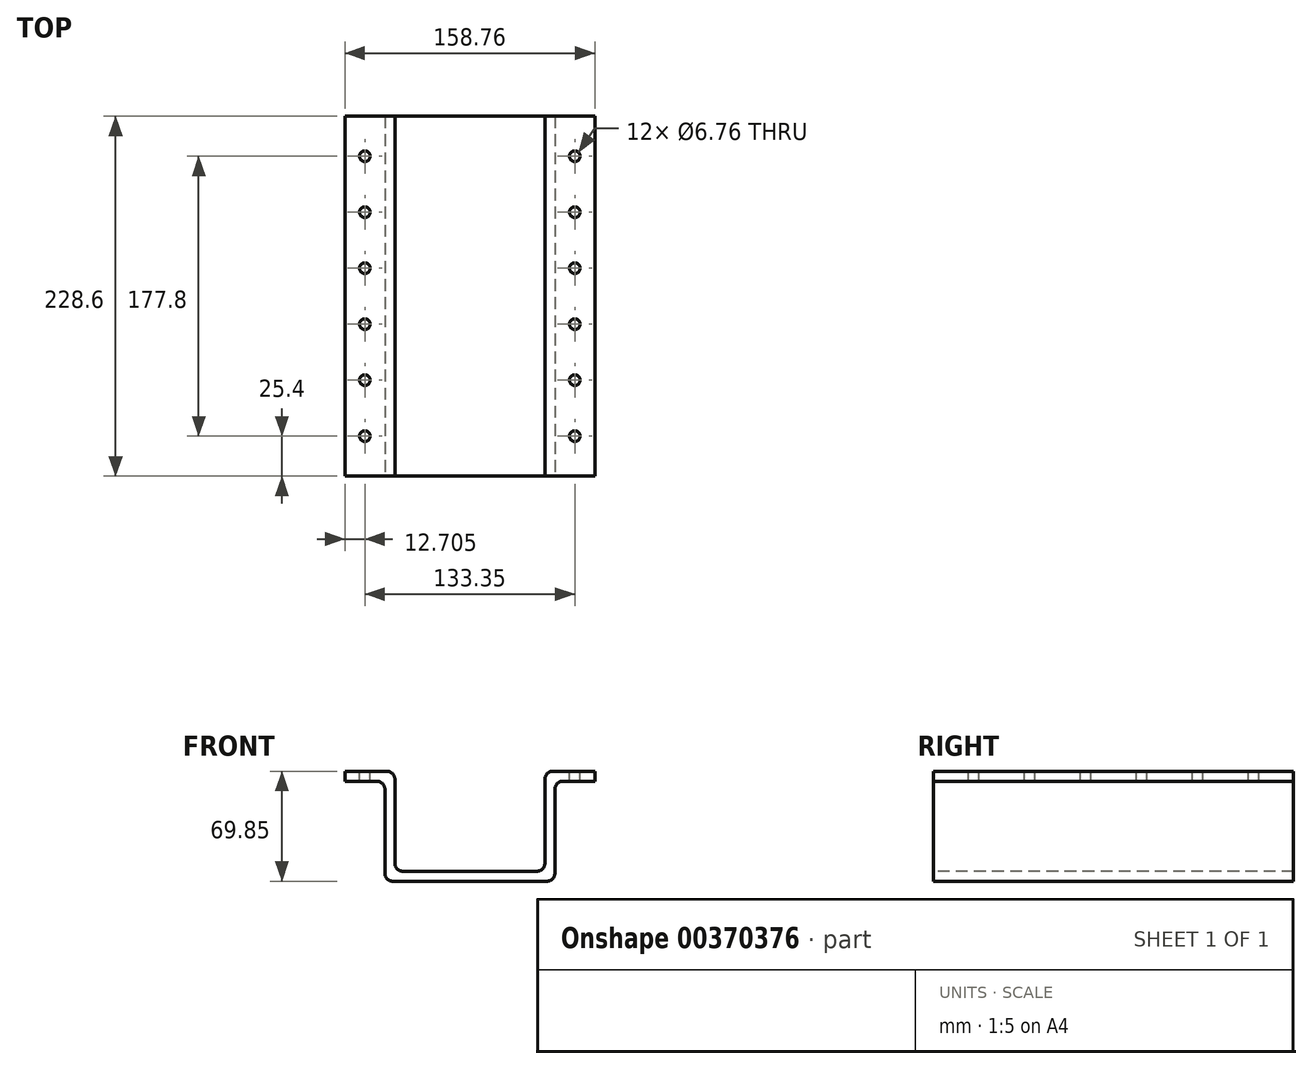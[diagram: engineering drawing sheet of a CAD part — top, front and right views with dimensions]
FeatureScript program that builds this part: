
annotation { "Feature Type Name" : "Feature", "Feature Type Description" : "" }
export const myFeature = defineFeature(function(context is Context, id is Id, definition is map)
    precondition{}
    {
        {
            var Q0;
            Q0=qCreatedBy(makeId("Front.planeOp"),FACE);
            var sketch = newSketch(context, id + "F0", { "sketchPlane" : qUnion([Q0])});
            skLineSegment(sketch, "E0", {"start": v(-53.98, 0) * mm, "end": v(53.98, 0) * mm});
            skLineSegment(sketch, "E1", {"start": v(-53.98, 0) * mm, "end": v(-53.97, 63.5) * mm});
            skLineSegment(sketch, "E2", {"start": v(-53.98, 63.5) * mm, "end": v(-79.38, 63.5) * mm});
            skLineSegment(sketch, "E3", {"start": v(-79.38, 63.5) * mm, "end": v(-79.38, 69.85) * mm});
            skLineSegment(sketch, "E4", {"start": v(-79.38, 69.85) * mm, "end": v(-47.63, 69.85) * mm});
            skLineSegment(sketch, "E5", {"start": v(-47.62, 69.85) * mm, "end": v(-47.62, 6.35) * mm});
            skLineSegment(sketch, "E6.MirrorCS", {"start": v(79.38, 63.5) * mm, "end": v(79.38, 69.85) * mm});
            skLineSegment(sketch, "E7.MirrorCS", {"start": v(53.98, 63.5) * mm, "end": v(79.38, 63.5) * mm});
            skLineSegment(sketch, "E8.MirrorCS", {"start": v(53.97, 0) * mm, "end": v(53.97, 63.5) * mm});
            skLineSegment(sketch, "E9.MirrorCS", {"start": v(47.62, 69.85) * mm, "end": v(47.62, 6.35) * mm});
            skLineSegment(sketch, "E10.MirrorCS", {"start": v(79.38, 69.85) * mm, "end": v(47.63, 69.85) * mm});
            skLineSegment(sketch, "E11", {"start": v(-47.62, 6.35) * mm, "end": v(47.62, 6.35) * mm});
            skSolve(sketch);
        }
        {
            var Q0;
            Q0=makeQuery(id+"F0.imprint","IMPRINT",FACE,{"disambiguationData":[TD([[makeQuery(id+"F0.imprint","IMPRINT",EDGE,{"derivedFrom":sQuery(id+"F0.wireOp",EDGE,"E0")}),1.0]])]});
            extrude(context, id + "F1", {"entities" : qUnion([Q0]), "oppositeDirection" : true, "depth" : 228.6 * mm});
        }
        {
            var Q0;
            Q0=qCreatedBy(makeId("Front.planeOp"),FACE);
            var sketch = newSketch(context, id + "F2", { "sketchPlane" : qUnion([Q0])});
            skLineSegment(sketch, "E12.0.0", {"start": v(53.97, 63.5) * mm, "end": v(79.38, 63.5) * mm, "construction": true});
            skLineSegment(sketch, "E12.0.1", {"start": v(79.38, 63.5) * mm, "end": v(79.38, 69.85) * mm, "construction": true});
            skLineSegment(sketch, "E12.0.2", {"start": v(79.38, 69.85) * mm, "end": v(47.62, 69.85) * mm, "construction": true});
            skLineSegment(sketch, "E12.0.3", {"start": v(47.62, 69.85) * mm, "end": v(47.62, 6.35) * mm, "construction": true});
            skLineSegment(sketch, "E12.0.4", {"start": v(47.62, 6.35) * mm, "end": v(-47.62, 6.35) * mm, "construction": true});
            skLineSegment(sketch, "E12.0.5", {"start": v(-47.62, 6.35) * mm, "end": v(-47.62, 69.85) * mm, "construction": true});
            skLineSegment(sketch, "E12.0.6", {"start": v(-47.63, 69.85) * mm, "end": v(-79.38, 69.85) * mm, "construction": true});
            skLineSegment(sketch, "E12.0.7", {"start": v(-79.38, 69.85) * mm, "end": v(-79.38, 63.5) * mm, "construction": true});
            skLineSegment(sketch, "E12.0.8", {"start": v(-79.38, 63.5) * mm, "end": v(-53.97, 63.5) * mm, "construction": true});
            skLineSegment(sketch, "E12.0.9", {"start": v(-53.97, 63.5) * mm, "end": v(-53.98, 0) * mm, "construction": true});
            skLineSegment(sketch, "E12.0.10", {"start": v(-53.98, 0) * mm, "end": v(53.98, 0) * mm, "construction": true});
            skLineSegment(sketch, "E12.0.11", {"start": v(53.97, 0) * mm, "end": v(53.97, 63.5) * mm, "construction": true});
            skLineSegment(sketch, "E13", {"start": v(-47.63, 57.15) * mm, "end": v(-18.3, 6.35) * mm});
            skLineSegment(sketch, "E14", {"start": v(-18.3, 6.35) * mm, "end": v(-47.62, 6.35) * mm});
            skLineSegment(sketch, "E15", {"start": v(-47.62, 57.15) * mm, "end": v(-47.62, 6.35) * mm});
            skSolve(sketch);
        }
        {
            var Q0;
            Q0=makeQuery(id+"F1.opExtrude","SWEPT_EDGE",EDGE,{"disambiguationData":[OSD([sQuery(id+"F0.wireOp",EDGE,"E4"),sQuery(id+"F0.wireOp",EDGE,"E5")])]});
            var Q1;
            Q1=makeQuery(id+"F1.opExtrude","SWEPT_EDGE",EDGE,{"disambiguationData":[OSD([sQuery(id+"F0.wireOp",EDGE,"E5"),sQuery(id+"F0.wireOp",EDGE,"E11")])]});
            var Q2;
            Q2=makeQuery(id+"F1.opExtrude","SWEPT_EDGE",EDGE,{"disambiguationData":[OSD([sQuery(id+"F0.wireOp",EDGE,"E0"),sQuery(id+"F0.wireOp",EDGE,"E8.MirrorCS")])]});
            var Q3;
            Q3=makeQuery(id+"F1.opExtrude","SWEPT_EDGE",EDGE,{"disambiguationData":[OSD([sQuery(id+"F0.wireOp",EDGE,"E9.MirrorCS"),sQuery(id+"F0.wireOp",EDGE,"E11")])]});
            var Q4;
            Q4=makeQuery(id+"F1.opExtrude","SWEPT_EDGE",EDGE,{"disambiguationData":[OSD([sQuery(id+"F0.wireOp",EDGE,"E0"),sQuery(id+"F0.wireOp",EDGE,"E1")])]});
            var Q5;
            Q5=makeQuery(id+"F1.opExtrude","SWEPT_EDGE",EDGE,{"disambiguationData":[OSD([sQuery(id+"F0.wireOp",EDGE,"E1"),sQuery(id+"F0.wireOp",EDGE,"E2")])]});
            var Q6;
            Q6=makeQuery(id+"F1.opExtrude","SWEPT_EDGE",EDGE,{"disambiguationData":[OSD([sQuery(id+"F0.wireOp",EDGE,"E7.MirrorCS"),sQuery(id+"F0.wireOp",EDGE,"E8.MirrorCS")])]});
            var Q7;
            Q7=makeQuery(id+"F1.opExtrude","SWEPT_EDGE",EDGE,{"disambiguationData":[OSD([sQuery(id+"F0.wireOp",EDGE,"E9.MirrorCS"),sQuery(id+"F0.wireOp",EDGE,"E10.MirrorCS")])]});
            fillet(context, id + "F3", {"entities" : qUnion([Q0, Q1, Q2, Q3, Q4, Q5, Q6, Q7]), "radius" : 5.08 * mm, "tangentPropagation" : true, "allowEdgeOverflow" : false});
        }
        {
            var Q0;
            Q0=makeQuery(id+"FtHRsgMsJNszQTX_1.boolean.opBoolean","MERGE",FACE,{"derivedFrom":[makeQuery(id+"F1.opExtrude","CAP_FACE",FACE,{"disambiguationData":[OSD([sQuery(id+"F0.wireOp",EDGE,"E0"),sQuery(id+"F0.wireOp",EDGE,"E1"),sQuery(id+"F0.wireOp",EDGE,"E2"),sQuery(id+"F0.wireOp",EDGE,"E3"),sQuery(id+"F0.wireOp",EDGE,"E4"),sQuery(id+"F0.wireOp",EDGE,"E5"),sQuery(id+"F0.wireOp",EDGE,"E6.MirrorCS"),sQuery(id+"F0.wireOp",EDGE,"E7.MirrorCS"),sQuery(id+"F0.wireOp",EDGE,"E8.MirrorCS"),sQuery(id+"F0.wireOp",EDGE,"E9.MirrorCS"),sQuery(id+"F0.wireOp",EDGE,"E10.MirrorCS"),sQuery(id+"F0.wireOp",EDGE,"E11")])],"isStart":true}),makeQuery(id+"FtHRsgMsJNszQTX_1.opExtrude","CAP_FACE",FACE,{"disambiguationData":[OSD([sQuery(id+"F2.wireOp",EDGE,"E13"),sQuery(id+"F2.wireOp",EDGE,"E14"),sQuery(id+"F2.wireOp",EDGE,"E15")])],"isStart":true})]});
            var sketch = newSketch(context, id + "F4", { "sketchPlane" : qUnion([Q0])});
            skLineSegment(sketch, "E16.0.0", {"start": v(-18.3, 6.35) * mm, "end": v(-47.63, 57.15) * mm, "construction": true});
            skLineSegment(sketch, "E16.0.1", {"start": v(-47.62, 57.15) * mm, "end": v(-47.62, 64.77) * mm, "construction": true});
            skArc(sketch, "E16.0.2", {"start": v(-47.62, 64.77) * mm, "mid": v(-49.11, 68.36) * mm, "end": v(-52.7, 69.85) * mm, "construction": true});
            skLineSegment(sketch, "E16.0.3", {"start": v(-52.7, 69.85) * mm, "end": v(-79.38, 69.85) * mm, "construction": true});
            skLineSegment(sketch, "E16.0.4", {"start": v(-79.38, 69.85) * mm, "end": v(-79.38, 63.5) * mm, "construction": true});
            skLineSegment(sketch, "E16.0.5", {"start": v(-79.38, 63.5) * mm, "end": v(-59.05, 63.5) * mm, "construction": true});
            skArc(sketch, "E16.0.6", {"start": v(-59.05, 63.5) * mm, "mid": v(-55.46, 62.01) * mm, "end": v(-53.97, 58.42) * mm, "construction": true});
            skLineSegment(sketch, "E16.0.7", {"start": v(-53.97, 58.42) * mm, "end": v(-53.98, 5.08) * mm, "construction": true});
            skArc(sketch, "E16.0.8", {"start": v(-53.98, 5.08) * mm, "mid": v(-52.49, 1.49) * mm, "end": v(-48.9, 0) * mm, "construction": true});
            skLineSegment(sketch, "E16.0.9", {"start": v(-48.9, 0) * mm, "end": v(48.9, 0) * mm, "construction": true});
            skArc(sketch, "E16.0.10", {"start": v(48.9, 0) * mm, "mid": v(52.49, 1.49) * mm, "end": v(53.97, 5.08) * mm, "construction": true});
            skLineSegment(sketch, "E16.0.11", {"start": v(53.97, 5.08) * mm, "end": v(53.97, 58.42) * mm, "construction": true});
            skArc(sketch, "E16.0.12", {"start": v(53.97, 58.42) * mm, "mid": v(55.46, 62.01) * mm, "end": v(59.05, 63.5) * mm, "construction": true});
            skLineSegment(sketch, "E16.0.13", {"start": v(59.05, 63.5) * mm, "end": v(79.38, 63.5) * mm, "construction": true});
            skLineSegment(sketch, "E16.0.14", {"start": v(79.38, 63.5) * mm, "end": v(79.38, 69.85) * mm, "construction": true});
            skLineSegment(sketch, "E16.0.15", {"start": v(79.38, 69.85) * mm, "end": v(52.7, 69.85) * mm, "construction": true});
            skArc(sketch, "E16.0.16", {"start": v(52.7, 69.85) * mm, "mid": v(49.11, 68.36) * mm, "end": v(47.62, 64.77) * mm, "construction": true});
            skLineSegment(sketch, "E16.0.17", {"start": v(47.62, 64.77) * mm, "end": v(47.62, 11.43) * mm, "construction": true});
            skArc(sketch, "E16.0.18", {"start": v(47.62, 11.43) * mm, "mid": v(46.14, 7.84) * mm, "end": v(42.55, 6.35) * mm, "construction": true});
            skLineSegment(sketch, "E16.0.19", {"start": v(42.55, 6.35) * mm, "end": v(-18.3, 6.35) * mm, "construction": true});
            skLineSegment(sketch, "E17", {"start": v(-47.63, 57.15) * mm, "end": v(-47.63, 6.35) * mm});
            skLineSegment(sketch, "E18", {"start": v(-47.63, 6.35) * mm, "end": v(-18.3, 6.35) * mm});
            skLineSegment(sketch, "E19", {"start": v(-47.62, 57.15) * mm, "end": v(-18.3, 6.35) * mm});
            skLineSegment(sketch, "E20.0", {"start": v(-41.27, 23.97) * mm, "end": v(-41.27, 15.24) * mm});
            skLineSegment(sketch, "E20.1", {"start": v(-31.5, 16.51) * mm, "end": v(-36.54, 25.24) * mm});
            skLineSegment(sketch, "E20.2", {"start": v(-38.73, 12.7) * mm, "end": v(-33.7, 12.7) * mm});
            skPoint(sketch, "E21.visualSharp", {"position": v(-41.27, 33.45) * mm});
            skArc(sketch, "E21.filletArc", {"start": v(-36.54, 25.24) * mm, "mid": v(-39.4, 26.43) * mm, "end": v(-41.27, 23.97) * mm});
            skPoint(sketch, "E22.visualSharp", {"position": v(-29.3, 12.7) * mm});
            skArc(sketch, "E22.filletArc", {"start": v(-33.7, 12.7) * mm, "mid": v(-31.5, 13.97) * mm, "end": v(-31.5, 16.51) * mm});
            skPoint(sketch, "E23.visualSharp", {"position": v(-41.27, 12.7) * mm});
            skArc(sketch, "E23.filletArc", {"start": v(-41.27, 15.24) * mm, "mid": v(-40.53, 13.44) * mm, "end": v(-38.73, 12.7) * mm});
            skSolve(sketch);
        }
        {
            var Q0;
            Q0=makeQuery(id+"F1.opExtrude","SWEPT_FACE",FACE,{"disambiguationData":[OSD([sQuery(id+"F0.wireOp",EDGE,"E4")])]});
            var sketch = newSketch(context, id + "F5", { "sketchPlane" : qUnion([Q0])});
            skLineSegment(sketch, "E24.0.0", {"start": v(-79.38, 0) * mm, "end": v(-52.7, 0) * mm, "construction": true});
            skLineSegment(sketch, "E24.0.1", {"start": v(-52.7, 0) * mm, "end": v(-52.7, 228.6) * mm, "construction": true});
            skLineSegment(sketch, "E24.0.2", {"start": v(-52.7, 228.6) * mm, "end": v(-79.38, 228.6) * mm, "construction": true});
            skLineSegment(sketch, "E24.0.3", {"start": v(-79.38, 228.6) * mm, "end": v(-79.38, 0) * mm, "construction": true});
            skPoint(sketch, "E25", {"position": v(-66.67, 203.2) * mm});
            skPoint(sketch, "E26.0.1.0", {"position": v(-66.67, 167.64) * mm});
            skPoint(sketch, "E26.0.2.0", {"position": v(-66.67, 132.08) * mm});
            skPoint(sketch, "E26.0.3.0", {"position": v(-66.67, 96.52) * mm});
            skPoint(sketch, "E26.0.4.0", {"position": v(-66.67, 60.96) * mm});
            skPoint(sketch, "E26.0.5.0", {"position": v(-66.67, 25.4) * mm});
            skLineSegment(sketch, "E26.direction1", {"start": v(-66.67, 203.2) * mm, "end": v(-66.67, 203.2) * mm});
            skLineSegment(sketch, "E26.direction2", {"start": v(-66.67, 203.2) * mm, "end": v(-66.67, 167.64) * mm, "construction": true});
            skLineSegment(sketch, "E27.0", {"start": v(-42.54, 228.6) * mm, "end": v(42.55, 228.6) * mm});
            skLineSegment(sketch, "E28", {"start": v(0, 228.6) * mm, "end": v(0, 250.77) * mm});
            skPoint(sketch, "E28.endSnap0", {"position": v(0, 228.6) * mm});
            skPoint(sketch, "E29.MirrorP", {"position": v(66.68, 167.64) * mm});
            skLineSegment(sketch, "E30.MirrorCS", {"start": v(66.68, 203.2) * mm, "end": v(66.68, 167.64) * mm, "construction": true});
            skPoint(sketch, "E31.MirrorP", {"position": v(66.67, 132.08) * mm});
            skPoint(sketch, "E32.MirrorP", {"position": v(66.67, 96.52) * mm});
            skPoint(sketch, "E33.MirrorP", {"position": v(66.67, 60.96) * mm});
            skPoint(sketch, "E34.MirrorP", {"position": v(66.67, 25.4) * mm});
            skSolve(sketch);
        }
        {
            var Q0;
            Q0=sQuery(id+"F5.wireOp",VERTEX,"E25");
            var Q1;
            Q1=sQuery(id+"F5.wireOp",VERTEX,"E26.0.1.0");
            var Q2;
            Q2=sQuery(id+"F5.wireOp",VERTEX,"E26.0.2.0");
            var Q3;
            Q3=sQuery(id+"F5.wireOp",VERTEX,"E26.0.3.0");
            var Q4;
            Q4=sQuery(id+"F5.wireOp",VERTEX,"E26.0.4.0");
            var Q5;
            Q5=sQuery(id+"F5.wireOp",VERTEX,"E26.0.5.0");
            var Q6;
            Q6=makeQuery(id+"F1.opExtrude","SWEPT_BODY",BODY,{"disambiguationData":[OSD([sQuery(id+"F0.wireOp",EDGE,"E0"),sQuery(id+"F0.wireOp",EDGE,"E1"),sQuery(id+"F0.wireOp",EDGE,"E2"),sQuery(id+"F0.wireOp",EDGE,"E3"),sQuery(id+"F0.wireOp",EDGE,"E4"),sQuery(id+"F0.wireOp",EDGE,"E5"),sQuery(id+"F0.wireOp",EDGE,"E6.MirrorCS"),sQuery(id+"F0.wireOp",EDGE,"E7.MirrorCS"),sQuery(id+"F0.wireOp",EDGE,"E8.MirrorCS"),sQuery(id+"F0.wireOp",EDGE,"E9.MirrorCS"),sQuery(id+"F0.wireOp",EDGE,"E10.MirrorCS"),sQuery(id+"F0.wireOp",EDGE,"E11")])]});
            hole(context, id + "F6", {"style" : HoleStyle.SIMPLE, "endStyle" : HoleEndStyle.THROUGH, "standardTappedOrClearance" : lookupTablePath({ "standard" : "ANSI", "fit" : "Normal (ASME)", "size" : "1/4", "type" : "Clearance" }), "standardBlindInLast" : lookupTablePath({ "fit" : "Free", "standard" : "ANSI", "size" : "1/4", "type" : "Clearance" }), "holeDiameter" : 6.76 * mm, "isTappedThrough" : true, "tappedDepth" : 25.4 * mm, "tapClearance" : 3, "locations" : qUnion([Q0, Q1, Q2, Q3, Q4, Q5]), "scope" : qUnion([Q6])});
        }
        {
            var Q0;
            Q0=sQuery(id+"F5.wireOp",VERTEX,"E30.MirrorCS.start");
            var Q1;
            Q1=sQuery(id+"F5.wireOp",VERTEX,"E29.MirrorP");
            var Q2;
            Q2=sQuery(id+"F5.wireOp",VERTEX,"E31.MirrorP");
            var Q3;
            Q3=sQuery(id+"F5.wireOp",VERTEX,"E32.MirrorP");
            var Q4;
            Q4=sQuery(id+"F5.wireOp",VERTEX,"E33.MirrorP");
            var Q5;
            Q5=sQuery(id+"F5.wireOp",VERTEX,"E34.MirrorP");
            var Q6;
            Q6=makeQuery(id+"F1.opExtrude","SWEPT_BODY",BODY,{"disambiguationData":[OSD([sQuery(id+"F0.wireOp",EDGE,"E0"),sQuery(id+"F0.wireOp",EDGE,"E1"),sQuery(id+"F0.wireOp",EDGE,"E2"),sQuery(id+"F0.wireOp",EDGE,"E3"),sQuery(id+"F0.wireOp",EDGE,"E4"),sQuery(id+"F0.wireOp",EDGE,"E5"),sQuery(id+"F0.wireOp",EDGE,"E6.MirrorCS"),sQuery(id+"F0.wireOp",EDGE,"E7.MirrorCS"),sQuery(id+"F0.wireOp",EDGE,"E8.MirrorCS"),sQuery(id+"F0.wireOp",EDGE,"E9.MirrorCS"),sQuery(id+"F0.wireOp",EDGE,"E10.MirrorCS"),sQuery(id+"F0.wireOp",EDGE,"E11")])]});
            hole(context, id + "F7", {"style" : HoleStyle.SIMPLE, "endStyle" : HoleEndStyle.THROUGH, "standardTappedOrClearance" : lookupTablePath({ "standard" : "ANSI", "fit" : "Normal (ASME)", "size" : "1/4", "type" : "Clearance" }), "standardBlindInLast" : lookupTablePath({ "fit" : "Free", "standard" : "ANSI", "size" : "1/4", "type" : "Clearance" }), "holeDiameter" : 6.76 * mm, "isTappedThrough" : true, "tappedDepth" : 25.4 * mm, "tapClearance" : 3, "locations" : qUnion([Q0, Q1, Q2, Q3, Q4, Q5]), "scope" : qUnion([Q6])});
        }
    });
